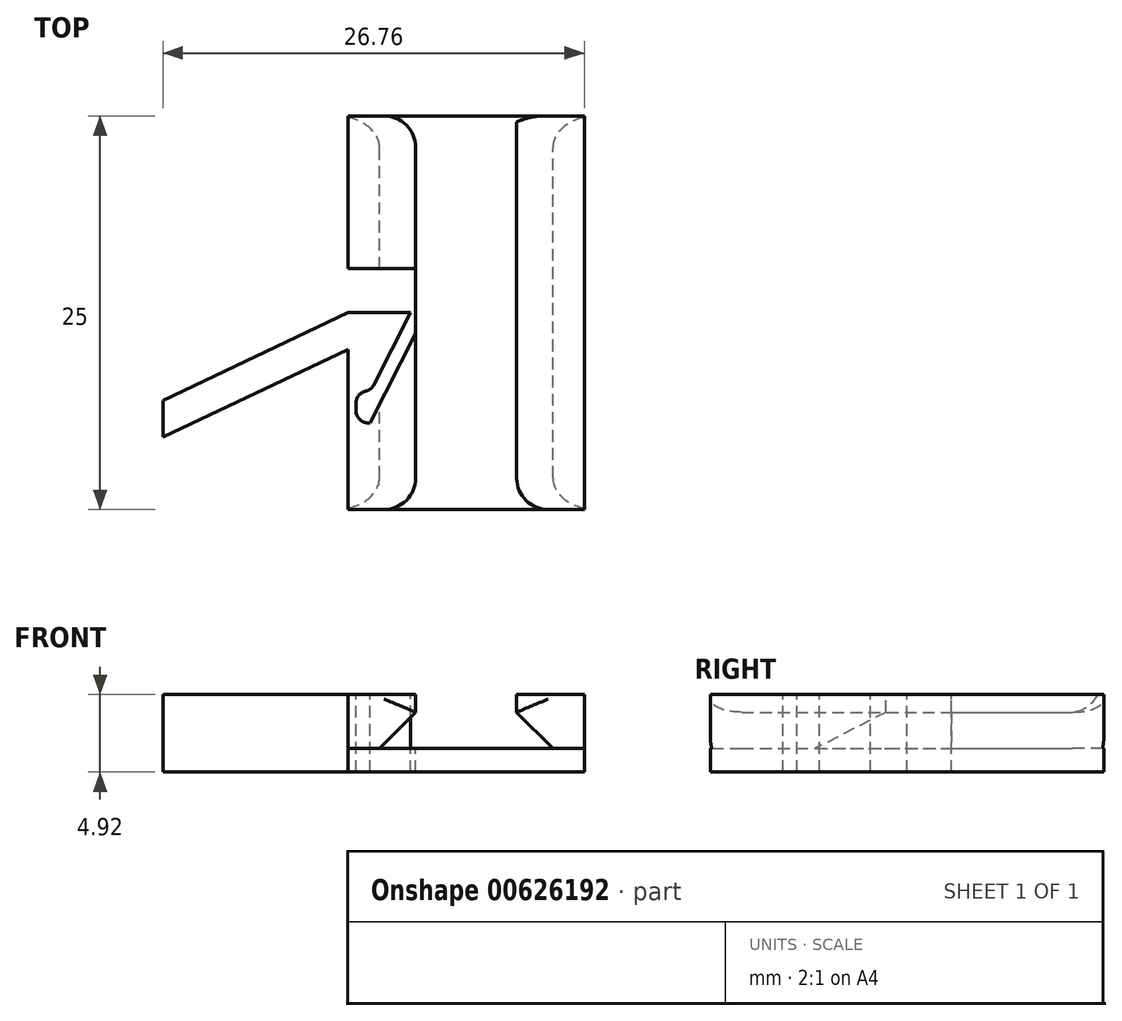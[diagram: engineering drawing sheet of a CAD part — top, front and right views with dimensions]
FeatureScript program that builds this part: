
annotation { "Feature Type Name" : "Feature", "Feature Type Description" : "" }
export const myFeature = defineFeature(function(context is Context, id is Id, definition is map)
    precondition{}
    {
        {
            var Q0;
            Q0=qCreatedBy(makeId("Front.planeOp"),FACE);
            var sketch = newSketch(context, id + "F0", { "sketchPlane" : qUnion([Q0])});
            skLineSegment(sketch, "E0", {"start": v(0, 0) * mm, "end": v(3, 0) * mm});
            skLineSegment(sketch, "E1", {"start": v(0, 0) * mm, "end": v(-3, 0) * mm});
            skLineSegment(sketch, "E2", {"start": v(-3, 0) * mm, "end": v(-3, -1) * mm});
            skLineSegment(sketch, "E3", {"start": v(-5, -3) * mm, "end": v(5, -3) * mm});
            skLineSegment(sketch, "E4", {"start": v(3, -1) * mm, "end": v(3, 0) * mm});
            skLineSegment(sketch, "E5", {"start": v(-3, -1) * mm, "end": v(-5, -3) * mm});
            skLineSegment(sketch, "E6", {"start": v(5, -3) * mm, "end": v(3, -1) * mm});
            skLineSegment(sketch, "E7", {"start": v(3, -1) * mm, "end": v(5, -1) * mm, "construction": true});
            skLineSegment(sketch, "E8", {"start": v(5, -1) * mm, "end": v(5, -3) * mm, "construction": true});
            skLineSegment(sketch, "E9", {"start": v(-5, -3) * mm, "end": v(-5, -1) * mm, "construction": true});
            skLineSegment(sketch, "E10", {"start": v(-5, -1) * mm, "end": v(-3, -1) * mm, "construction": true});
            skLineSegment(sketch, "E11.0", {"start": v(-3.2, 0.2) * mm, "end": v(-3.2, -0.91) * mm});
            skLineSegment(sketch, "E11.1", {"start": v(0, 0.21) * mm, "end": v(-3.2, 0.2) * mm});
            skLineSegment(sketch, "E11.2", {"start": v(0, 0.21) * mm, "end": v(3.2, 0.21) * mm});
            skLineSegment(sketch, "E11.3", {"start": v(3.2, -0.91) * mm, "end": v(3.2, 0.21) * mm});
            skLineSegment(sketch, "E12.0", {"start": v(5.5, -3.2) * mm, "end": v(3.2, -0.91) * mm});
            skLineSegment(sketch, "E12.1", {"start": v(-5.5, -3.21) * mm, "end": v(5.5, -3.2) * mm});
            skLineSegment(sketch, "E12.2", {"start": v(-3.2, -0.91) * mm, "end": v(-5.5, -3.21) * mm});
            skLineSegment(sketch, "E13.bottom", {"start": v(-7.5, 0.2) * mm, "end": v(7.5, 0.2) * mm});
            skLineSegment(sketch, "E13.top", {"start": v(-7.5, -4.71) * mm, "end": v(7.5, -4.71) * mm});
            skLineSegment(sketch, "E13.left", {"start": v(-7.5, 0.2) * mm, "end": v(-7.5, -4.71) * mm});
            skLineSegment(sketch, "E13.right", {"start": v(7.5, 0.2) * mm, "end": v(7.5, -4.71) * mm});
            skSolve(sketch);
        }
        {
            var Q0;
            {var subQ1=sQuery(id+"F0.wireOp",EDGE,"E11.0");Q0=makeQuery(id+"F0.imprint","IMPRINT",FACE,{"disambiguationData":[TD([[makeQuery(id+"F0.imprint","IMPRINT",EDGE,{"derivedFrom":subQ1}),-1.0]])]});}
            extrude(context, id + "F1", {"entities" : qUnion([Q0]), "depth" : 25 * mm, "offsetDistance" : 25 * mm});
        }
        {
            var Q0;
            {var subQ0=sQuery(id+"F0.wireOp",EDGE,"E13.bottom");Q0=makeQuery(id+"F1.opExtrude","SWEPT_FACE",FACE,{"disambiguationData":[OSD([subQ0]),TDD([makeQuery(id+"F0.imprint","IMPRINT",EDGE,{"disambiguationData":[TD([[makeQuery(id+"F0.imprint","INTERSECT",VERTEX,{"derivedFrom":[sQuery(id+"F0.wireOp",EDGE,"E11.0"),subQ0]}),1.0]])],"derivedFrom":subQ0})])]});}
            var sketch = newSketch(context, id + "F2", { "sketchPlane" : qUnion([Q0])});
            skLineSegment(sketch, "E14", {"start": v(-7.5, -12.5) * mm, "end": v(-3.53, -12.5) * mm});
            skPoint(sketch, "E15", {"position": v(-3.2, -12.5) * mm});
            skLineSegment(sketch, "E16", {"start": v(-3.53, -12.5) * mm, "end": v(-6.08, -17.5) * mm});
            skLineSegment(sketch, "E17", {"start": v(-7.5, -12.5) * mm, "end": v(-7.5, -19.5) * mm});
            skLineSegment(sketch, "E18", {"start": v(-7.5, -12.5) * mm, "end": v(-19.25, -18.07) * mm});
            skLineSegment(sketch, "E19.0", {"start": v(-7.5, -14.82) * mm, "end": v(-19.25, -20.4) * mm});
            skLineSegment(sketch, "E20", {"start": v(-19.25, -18.07) * mm, "end": v(-19.25, -20.4) * mm});
            skLineSegment(sketch, "E21.top", {"start": v(-7.5, -9.7) * mm, "end": v(-2.23, -9.7) * mm});
            skLineSegment(sketch, "E21.left", {"start": v(-7.5, -19.5) * mm, "end": v(-7.5, -9.7) * mm});
            skLineSegment(sketch, "E22", {"start": v(-6.1, -19.5) * mm, "end": v(-2.23, -11.92) * mm});
            skLineSegment(sketch, "E23", {"start": v(-2.23, -11.92) * mm, "end": v(-2.23, -9.7) * mm});
            skLineSegment(sketch, "E24", {"start": v(-7.5, -19.5) * mm, "end": v(-6.1, -19.5) * mm});
            skLineSegment(sketch, "E25", {"start": v(-6.08, -17.5) * mm, "end": v(-7.5, -17.5) * mm});
            skLineSegment(sketch, "E26", {"start": v(-7, -17.5) * mm, "end": v(-7, -19.5) * mm});
            skCircle(sketch, "E27", {"center": v(-7.5, -12.5) * mm, "radius": 3.98 * mm, "construction": true});
            skSolve(sketch);
        }
        {
            var Q0;
            {var subQ0=sQuery(id+"F2.wireOp",EDGE,"E21.left");var subQ1=sQuery(id+"F2.wireOp",EDGE,"E14");var subQ2=makeQuery(id+"F2.imprint","INTERSECT",VERTEX,{"derivedFrom":[subQ1,sQuery(id+"F2.wireOp",EDGE,"E18"),subQ0]});Q0=makeQuery(id+"F2.imprint","IMPRINT",FACE,{"disambiguationData":[TD([[makeQuery(id+"F2.imprint","IMPRINT",EDGE,{"disambiguationData":[TD([[subQ2,-1.0]])],"derivedFrom":subQ1}),1.0]])]});}
            var Q1;
            {var subQ0=sQuery(id+"F2.wireOp",EDGE,"E21.right");Q1=makeQuery(id+"F2.imprint","IMPRINT",FACE,{"disambiguationData":[TD([[makeQuery(id+"F2.imprint","IMPRINT",EDGE,{"derivedFrom":subQ0}),1.0]])]});}
            var Q2;
            {var subQ0=sQuery(id+"F2.wireOp",EDGE,"E21.bottom");var subQ1=sQuery(id+"F2.wireOp",EDGE,"E16");var subQ2=makeQuery(id+"F2.imprint","INTERSECT",VERTEX,{"derivedFrom":[subQ1,subQ0]});Q2=makeQuery(id+"F2.imprint","IMPRINT",FACE,{"disambiguationData":[TD([[makeQuery(id+"F2.imprint","IMPRINT",EDGE,{"disambiguationData":[TD([[subQ2,1.0]])],"derivedFrom":subQ1}),1.0]])]});}
            var Q3;
            {var subQ0=sQuery(id+"F2.wireOp",EDGE,"PWb94c2L-cldH-c0YX-Mz9c-UrDzxOQ2ht7D");Q3=makeQuery(id+"F2.imprint","IMPRINT",FACE,{"disambiguationData":[TD([[makeQuery(id+"F2.imprint","IMPRINT",EDGE,{"derivedFrom":subQ0}),1.0]])]});}
            var Q4;
            {var subQ0=sQuery(id+"F2.wireOp",EDGE,"MEwXAGkM-ULK5-K2g6-X4UN-puUbbASLgv2R");Q4=makeQuery(id+"F2.imprint","IMPRINT",FACE,{"disambiguationData":[TD([[makeQuery(id+"F2.imprint","IMPRINT",EDGE,{"derivedFrom":subQ0}),-1.0]])]});}
            extrude(context, id + "F3", {"entities" : qUnion([Q0, Q1, Q2, Q3, Q4]), "operationType" : NewBodyOperationType.REMOVE, "oppositeDirection" : true, "depth" : 25 * mm, "offsetDistance" : 25 * mm});
        }
        {
            var Q0;
            {var subQ0=sQuery(id+"F2.wireOp",EDGE,"E18");Q0=makeQuery(id+"F2.imprint","IMPRINT",FACE,{"disambiguationData":[TD([[makeQuery(id+"F2.imprint","IMPRINT",EDGE,{"derivedFrom":subQ0}),1.0]])]});}
            var Q1;
            {var subQ0=sQuery(id+"F2.wireOp",EDGE,"w3vLhJVO-UcQZ-AZ36-s9KB-ZPBySBapqTD3");Q1=makeQuery(id+"F2.imprint","IMPRINT",FACE,{"disambiguationData":[TD([[makeQuery(id+"F2.imprint","IMPRINT",EDGE,{"derivedFrom":subQ0}),1.0]])]});}
            var Q2;
            {var subQ1=sQuery(id+"F2.wireOp",EDGE,"E14");Q2=makeQuery(id+"F2.imprint","IMPRINT",FACE,{"disambiguationData":[TD([[makeQuery(id+"F2.imprint","IMPRINT",EDGE,{"derivedFrom":subQ1}),-1.0]])]});}
            extrude(context, id + "F4", {"entities" : qUnion([Q0, Q1, Q2]), "operationType" : NewBodyOperationType.ADD, "oppositeDirection" : true, "depth" : 4.92 * mm, "offsetDistance" : 25 * mm});
        }
        {
            var Q0;
            Q0=makeQuery(id+"F1.opExtrude","CAP_EDGE",EDGE,{"disambiguationData":[OSD([sQuery(id+"F0.wireOp",EDGE,"E12.2")])],"isStart":false});
            var Q1;
            Q1=makeQuery(id+"F1.opExtrude","CAP_EDGE",EDGE,{"disambiguationData":[OSD([sQuery(id+"F0.wireOp",EDGE,"E11.0")])],"isStart":false});
            var Q2;
            Q2=makeQuery(id+"F1.opExtrude","CAP_EDGE",EDGE,{"disambiguationData":[OSD([sQuery(id+"F0.wireOp",EDGE,"E11.3")])],"isStart":false});
            var Q3;
            Q3=makeQuery(id+"F1.opExtrude","CAP_EDGE",EDGE,{"disambiguationData":[OSD([sQuery(id+"F0.wireOp",EDGE,"E12.0")])],"isStart":false});
            var Q4;
            Q4=makeQuery(id+"F1.opExtrude","CAP_EDGE",EDGE,{"disambiguationData":[OSD([sQuery(id+"F0.wireOp",EDGE,"E12.0")])],"isStart":true});
            var Q5;
            Q5=makeQuery(id+"F1.opExtrude","CAP_EDGE",EDGE,{"disambiguationData":[OSD([sQuery(id+"F0.wireOp",EDGE,"E12.2")])],"isStart":true});
            var Q6;
            Q6=makeQuery(id+"F1.opExtrude","CAP_EDGE",EDGE,{"disambiguationData":[OSD([sQuery(id+"F0.wireOp",EDGE,"E11.0")])],"isStart":true});
            fillet(context, id + "F5", {"entities" : qUnion([Q0, Q1, Q2, Q3, Q4, Q5, Q6]), "radius" : 2 * mm, "tangentPropagation" : true, "allowEdgeOverflow" : false});
        }
        {
            var Q0;
            {var subQ0=sQuery(id+"F0.wireOp",EDGE,"E11.0");var subQ1=sQuery(id+"F2.wireOp",EDGE,"E22");Q0=makeQuery(id+"F3.boolean.opBoolean","COPY",EDGE,{"disambiguationData":[topologyDisambiguationEdgeConnected([makeQuery(id+"F1.opExtrude","SWEPT_FACE",FACE,{"disambiguationData":[OSD([subQ0])]})])],"derivedFrom":makeQuery(id+"F3.opExtrude","SWEPT_EDGE",EDGE,{"disambiguationData":[OSD([subQ0,sQuery(id+"F0.wireOp",EDGE,"E13.bottom"),subQ1])]})});}
            fillet(context, id + "F6", {"entities" : qUnion([Q0]), "radius" : 0.51 * mm, "tangentPropagation" : true, "allowEdgeOverflow" : false});
        }
        {
            var Q0;
            Q0=makeQuery(id+"F3.boolean.opBoolean","COPY",EDGE,{"derivedFrom":makeQuery(id+"F3.opExtrude","SWEPT_EDGE",EDGE,{"disambiguationData":[OSD([sQuery(id+"F2.wireOp",EDGE,"E16"),sQuery(id+"F2.wireOp",EDGE,"E25")])]})});
            fillet(context, id + "F7", {"entities" : qUnion([Q0]), "radius" : 0.7 * mm, "tangentPropagation" : true, "allowEdgeOverflow" : false});
        }
        {
            var Q0;
            Q0=makeQuery(id+"F3.boolean.opBoolean","COPY",EDGE,{"derivedFrom":makeQuery(id+"F3.opExtrude","SWEPT_EDGE",EDGE,{"disambiguationData":[OSD([sQuery(id+"F2.wireOp",EDGE,"E25"),sQuery(id+"F2.wireOp",EDGE,"E26")])]})});
            var Q1;
            Q1=makeQuery(id+"F3.boolean.opBoolean","COPY",EDGE,{"derivedFrom":makeQuery(id+"F3.opExtrude","SWEPT_EDGE",EDGE,{"disambiguationData":[OSD([sQuery(id+"F2.wireOp",EDGE,"E24"),sQuery(id+"F2.wireOp",EDGE,"E26")])]})});
            fillet(context, id + "F8", {"entities" : qUnion([Q0, Q1]), "radius" : 0.77 * mm, "tangentPropagation" : true, "allowEdgeOverflow" : false});
        }
    });
